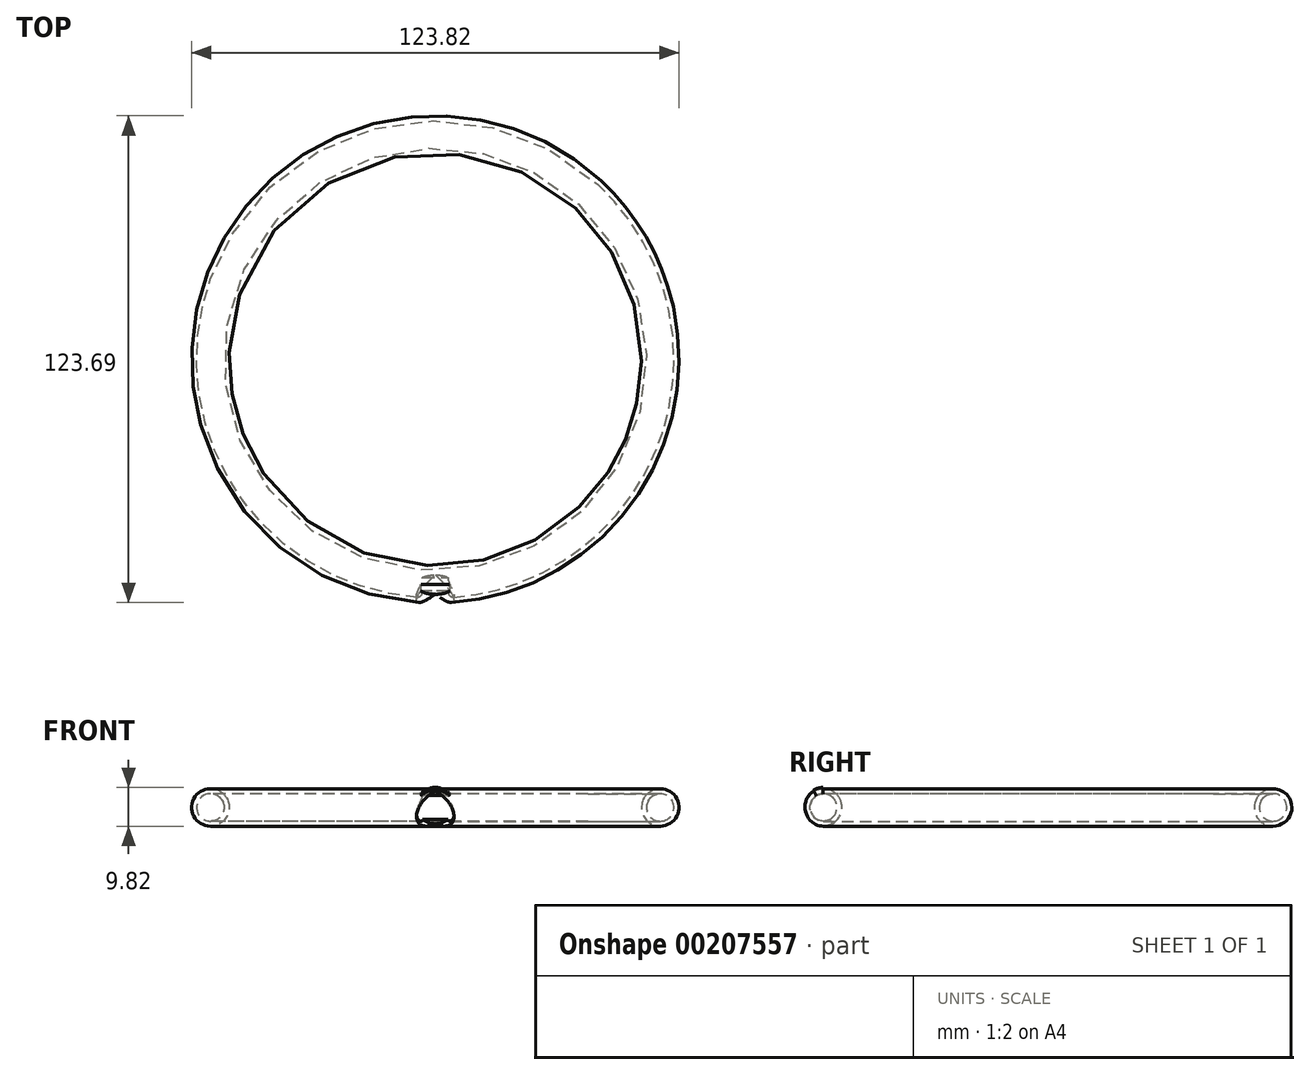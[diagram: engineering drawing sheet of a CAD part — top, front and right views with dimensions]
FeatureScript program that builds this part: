
annotation { "Feature Type Name" : "Feature", "Feature Type Description" : "" }
export const myFeature = defineFeature(function(context is Context, id is Id, definition is map)
    precondition{}
    {
        {
            var Q0;
            Q0=qCreatedBy(makeId("Front.planeOp"),FACE);
            var sketch = newSketch(context, id + "F0", { "sketchPlane" : qUnion([Q0])});
            skLineSegment(sketch, "E0", {"start": v(0, 0) * mm, "end": v(-57.15, 0) * mm, "construction": true});
            skCircle(sketch, "E1", {"center": v(-57.15, 0) * mm, "radius": 3.5 * mm});
            skCircle(sketch, "E2", {"center": v(-57.15, 0) * mm, "radius": 4.76 * mm});
            skLineSegment(sketch, "E3", {"start": v(0, 0) * mm, "end": v(0, 11.57) * mm, "construction": true});
            skSolve(sketch);
        }
        {
            var Q0;
            Q0=makeQuery(id+"F0.imprint","IMPRINT",FACE,{"disambiguationData":[TD([[makeQuery(id+"F0.imprint","IMPRINT",EDGE,{"derivedFrom":sQuery(id+"F0.wireOp",EDGE,"E1")}),-1.0]])]});
            var Q1;
            Q1=sQuery(id+"F0.wireOp",EDGE,"E3");
            revolve(context, id + "F1", {"entities" : qUnion([Q0]), "axis" : qUnion([Q1]), "revolveType" : RevolveType.FULL});
        }
        {
            var Q0;
            Q0=qCreatedBy(makeId("Front.planeOp"),FACE);
            cPlane(context, id + "F2", {"entities" : qUnion([Q0]), "cplaneType" : CPlaneType.OFFSET, "offset" : 57.15 * mm, "width" : 152.4 * mm, "height" : 152.4 * mm});
        }
        {
            var Q0;
            Q0=qCreatedBy(id+"F2.planeOp",FACE);
            var sketch = newSketch(context, id + "F3", { "sketchPlane" : qUnion([Q0])});
            skArc(sketch, "E4", {"start": v(5.06, 0) * mm, "mid": v(0, 5.06) * mm, "end": v(-5.06, 0) * mm});
            skLineSegment(sketch, "E5", {"start": v(-5.06, 0) * mm, "end": v(5.06, 0) * mm});
            skSolve(sketch);
        }
        {
            var Q0;
            Q0=qSketchRegion(id+"F3",true);
            var Q1;
            Q1=sQuery(id+"F3.wireOp",EDGE,"E5");
            revolve(context, id + "F4", {"entities" : qUnion([Q0]), "axis" : qUnion([Q1]), "revolveType" : RevolveType.ONE_DIRECTION, "angle" : 30 * degree});
        }
        {
            var Q0;
            Q0=makeQuery(id+"F4.opRevolve","CAP_FACE",FACE,{"disambiguationData":[OSD([sQuery(id+"F3.wireOp",EDGE,"E4"),sQuery(id+"F3.wireOp",EDGE,"E5")])],"isStart":false});
            var sketch = newSketch(context, id + "F5", { "sketchPlane" : qUnion([Q0])});
            skCircle(sketch, "E6", {"center": v(0, 28.57) * mm, "radius": 3.5 * mm});
            skCircle(sketch, "E7", {"center": v(0, 28.57) * mm, "radius": 4.76 * mm});
            skSolve(sketch);
        }
        {
            var Q0;
            Q0=qSketchRegion(id+"F5",true);
            extrude(context, id + "F6", {"entities" : qUnion([Q0]), "offsetDistance" : 25.4 * mm, "depth" : 25.4 * mm});
        }
        {
            var Q0;
            {var subQ0=sQuery(id+"F5.wireOp",EDGE,"E6");var subQ1=makeQuery(id+"F4.opRevolve","CAP_EDGE",EDGE,{"disambiguationData":[OSD([sQuery(id+"F3.wireOp",EDGE,"E5")])],"isStart":true});var subQ2=makeQuery(id+"F5.imprint","INTERSECT",VERTEX,{"disambiguationData":[OD(0.0)],"derivedFrom":[subQ1,subQ0]});Q0=makeQuery(id+"F5.imprint","IMPRINT",FACE,{"disambiguationData":[TD([[makeQuery(id+"F5.imprint","IMPRINT",EDGE,{"disambiguationData":[TD([[subQ2,1.0]])],"derivedFrom":subQ0}),1.0]])]});}
            var Q1;
            {var subQ0=sQuery(id+"F5.wireOp",EDGE,"E6");var subQ1=makeQuery(id+"F4.opRevolve","CAP_EDGE",EDGE,{"disambiguationData":[OSD([sQuery(id+"F3.wireOp",EDGE,"E5")])],"isStart":true});var subQ2=makeQuery(id+"F5.imprint","INTERSECT",VERTEX,{"disambiguationData":[OD(0.0)],"derivedFrom":[subQ1,subQ0]});Q1=makeQuery(id+"F5.imprint","IMPRINT",FACE,{"disambiguationData":[TD([[makeQuery(id+"F5.imprint","IMPRINT",EDGE,{"disambiguationData":[TD([[subQ2,-1.0]])],"derivedFrom":subQ0}),1.0]])]});}
            var Q2;
            {var subQ0=sQuery(id+"F5.wireOp",EDGE,"E6");var subQ1=makeQuery(id+"F4.opRevolve","CAP_EDGE",EDGE,{"disambiguationData":[OSD([sQuery(id+"F3.wireOp",EDGE,"E5")])],"isStart":true});var subQ2=makeQuery(id+"F5.imprint","INTERSECT",VERTEX,{"disambiguationData":[OD(0.0)],"derivedFrom":[subQ1,subQ0]});Q2=makeQuery(id+"F5.imprint","IMPRINT",FACE,{"disambiguationData":[TD([[makeQuery(id+"F5.imprint","IMPRINT",EDGE,{"disambiguationData":[TD([[subQ2,-1.0]])],"derivedFrom":subQ0}),-1.0]])]});}
            var Q3;
            {var subQ0=sQuery(id+"F5.wireOp",EDGE,"E6");var subQ1=makeQuery(id+"F4.opRevolve","CAP_EDGE",EDGE,{"disambiguationData":[OSD([sQuery(id+"F3.wireOp",EDGE,"E5")])],"isStart":true});var subQ2=makeQuery(id+"F5.imprint","INTERSECT",VERTEX,{"disambiguationData":[OD(0.0)],"derivedFrom":[subQ1,subQ0]});Q3=makeQuery(id+"F5.imprint","IMPRINT",FACE,{"disambiguationData":[TD([[makeQuery(id+"F5.imprint","IMPRINT",EDGE,{"disambiguationData":[TD([[subQ2,1.0]])],"derivedFrom":subQ0}),-1.0]])]});}
            extrude(context, id + "F7", {"entities" : qUnion([Q0, Q1, Q2, Q3]), "operationType" : NewBodyOperationType.REMOVE, "depth" : 25.4 * mm});
        }
        {
            var Q0;
            Q0=makeQuery(id+"F0.imprint","IMPRINT",FACE,{"disambiguationData":[TD([[makeQuery(id+"F0.imprint","IMPRINT",EDGE,{"derivedFrom":sQuery(id+"F0.wireOp",EDGE,"E1")}),1.0]])]});
            var Q1;
            Q1=sQuery(id+"F0.wireOp",EDGE,"E3");
            revolve(context, id + "F8", {"operationType" : NewBodyOperationType.REMOVE, "entities" : qUnion([Q0]), "axis" : qUnion([Q1]), "revolveType" : RevolveType.FULL, "oppositeDirection" : true});
        }
    });
